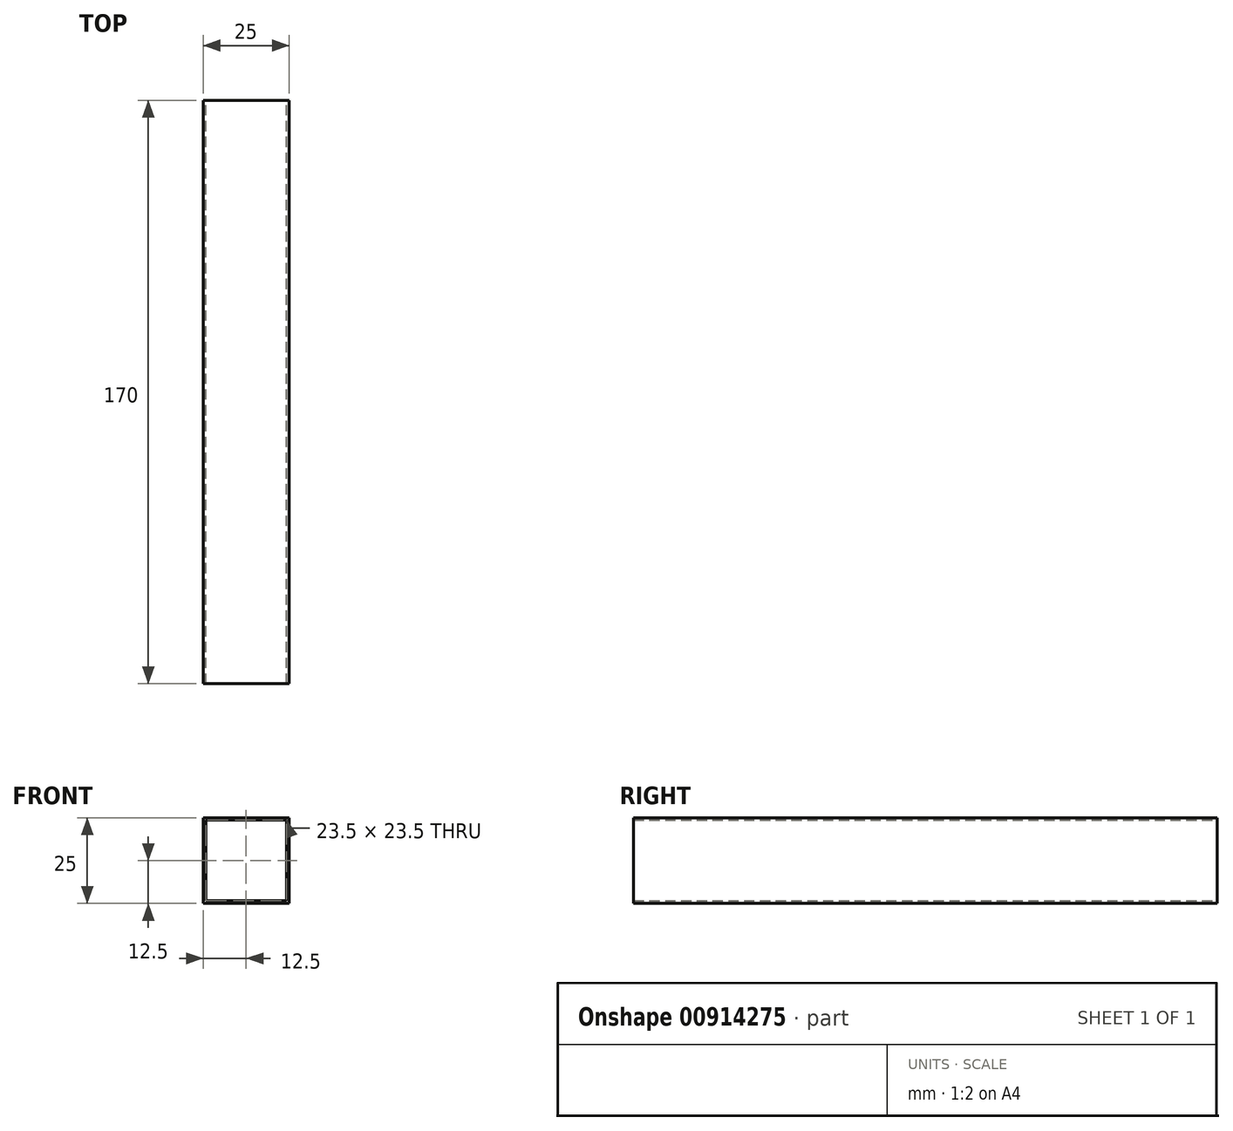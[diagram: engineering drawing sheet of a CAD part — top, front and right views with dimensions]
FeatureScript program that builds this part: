
annotation { "Feature Type Name" : "Feature", "Feature Type Description" : "" }
export const myFeature = defineFeature(function(context is Context, id is Id, definition is map)
    precondition{}
    {
        {
            var Q0;
            Q0=qCreatedBy(makeId("Front.planeOp"),FACE);
            var sketch = newSketch(context, id + "F0", { "sketchPlane" : qUnion([Q0])});
            skLineSegment(sketch, "E0.bottom", {"start": v(12.5, 12.5) * mm, "end": v(-12.5, 12.5) * mm});
            skLineSegment(sketch, "E0.top", {"start": v(12.5, -12.5) * mm, "end": v(-12.5, -12.5) * mm});
            skLineSegment(sketch, "E0.left", {"start": v(12.5, 12.5) * mm, "end": v(12.5, -12.5) * mm});
            skLineSegment(sketch, "E0.right", {"start": v(-12.5, 12.5) * mm, "end": v(-12.5, -12.5) * mm});
            skPoint(sketch, "E0.middle", {"position": v(0, 0) * mm});
            skLineSegment(sketch, "E1.bottom", {"start": v(11.75, 11.75) * mm, "end": v(-11.75, 11.75) * mm});
            skLineSegment(sketch, "E1.top", {"start": v(11.75, -11.75) * mm, "end": v(-11.75, -11.75) * mm});
            skLineSegment(sketch, "E1.left", {"start": v(11.75, 11.75) * mm, "end": v(11.75, -11.75) * mm});
            skLineSegment(sketch, "E1.right", {"start": v(-11.75, 11.75) * mm, "end": v(-11.75, -11.75) * mm});
            skSolve(sketch);
        }
        {
            var Q0;
            Q0=makeQuery(id+"F0.imprint","IMPRINT",FACE,{"disambiguationData":[TD([[makeQuery(id+"F0.imprint","IMPRINT",EDGE,{"derivedFrom":sQuery(id+"F0.wireOp",EDGE,"E0.bottom")}),1.0]])]});
            extrude(context, id + "F1", {"entities" : qUnion([Q0]), "depth" : 170 * mm, "offsetDistance" : 25 * mm});
        }
    });
